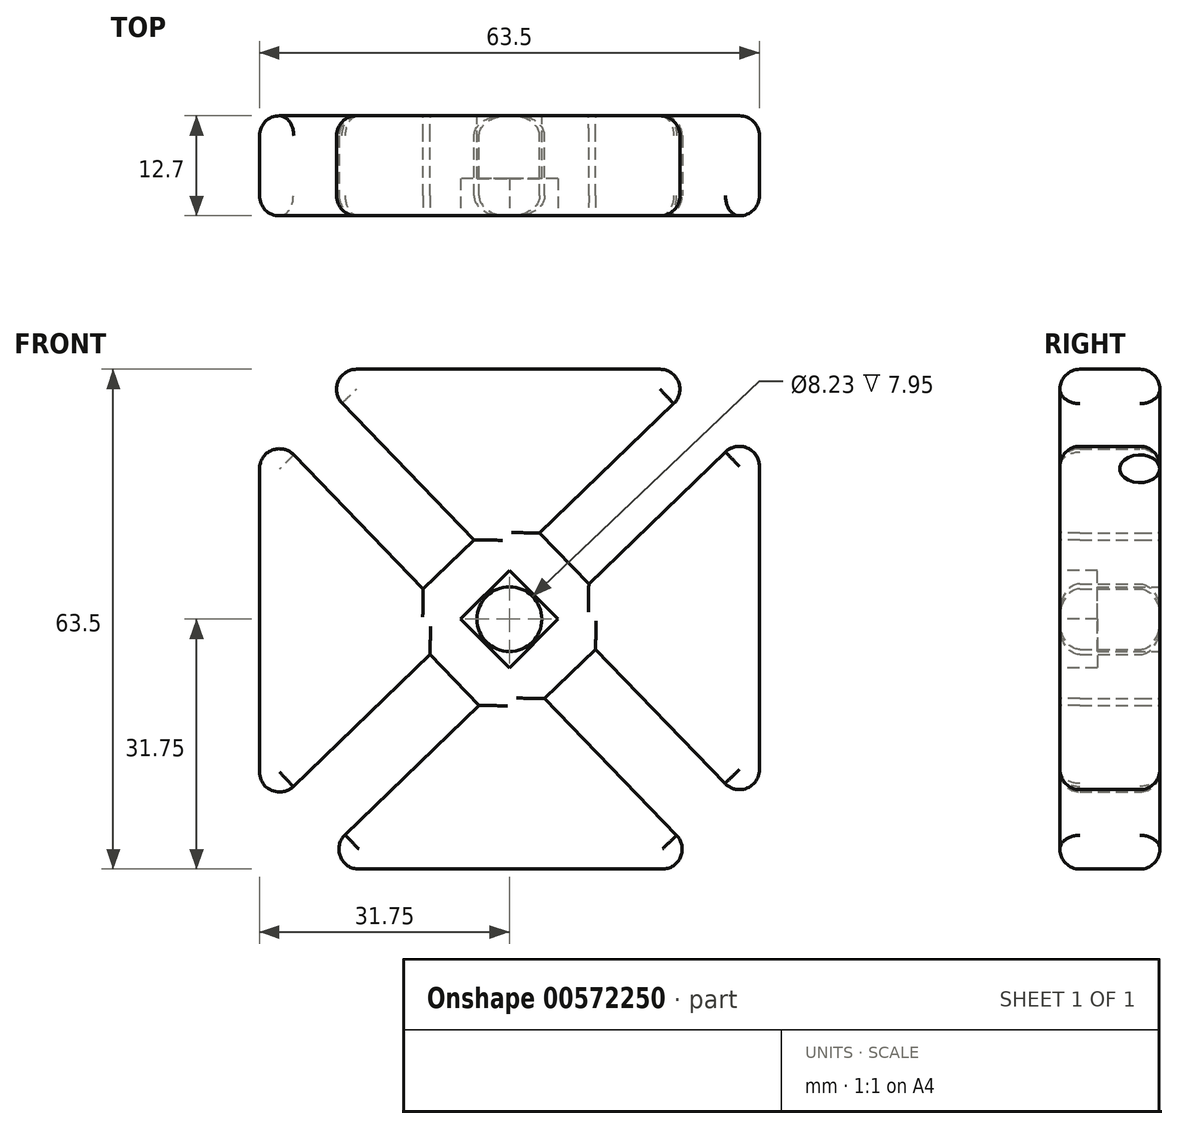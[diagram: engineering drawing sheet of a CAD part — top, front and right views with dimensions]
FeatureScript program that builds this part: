
annotation { "Feature Type Name" : "Feature", "Feature Type Description" : "" }
export const myFeature = defineFeature(function(context is Context, id is Id, definition is map)
    precondition{}
    {
        {
            var Q0;
            Q0=qCreatedBy(makeId("Front.planeOp"),FACE);
            var sketch = newSketch(context, id + "F0", { "sketchPlane" : qUnion([Q0])});
            skLineSegment(sketch, "E0.bottom", {"start": v(0, 0) * mm, "end": v(63.5, 0) * mm});
            skLineSegment(sketch, "E0.top", {"start": v(0, 63.5) * mm, "end": v(63.5, 63.5) * mm});
            skLineSegment(sketch, "E0.left", {"start": v(0, 0) * mm, "end": v(0, 63.5) * mm});
            skLineSegment(sketch, "E0.right", {"start": v(63.5, 0) * mm, "end": v(63.5, 63.5) * mm});
            skCircle(sketch, "E1", {"center": v(31.75, 31.75) * mm, "radius": 4.11 * mm});
            skPoint(sketch, "E1.centerSnap0", {"position": v(0, 31.75) * mm});
            skPoint(sketch, "E1.centerSnap1", {"position": v(31.75, 0) * mm});
            skLineSegment(sketch, "E2", {"start": v(0, 57.15) * mm, "end": v(20.8, 35.6) * mm});
            skLineSegment(sketch, "E3", {"start": v(20.8, 35.6) * mm, "end": v(27.26, 41.83) * mm});
            skLineSegment(sketch, "E4", {"start": v(27.26, 41.83) * mm, "end": v(6.35, 63.5) * mm});
            skPoint(sketch, "E5.startSnap0", {"position": v(63.5, 31.75) * mm});
            skPoint(sketch, "E6.startSnap0", {"position": v(31.75, 63.5) * mm});
            skLineSegment(sketch, "E7.1.0", {"start": v(27.9, 20.8) * mm, "end": v(21.67, 27.26) * mm});
            skLineSegment(sketch, "E7.1.1", {"start": v(21.67, 27.26) * mm, "end": v(0, 6.35) * mm});
            skLineSegment(sketch, "E7.1.2", {"start": v(6.35, 0) * mm, "end": v(27.9, 20.8) * mm});
            skLineSegment(sketch, "E7.2.0", {"start": v(42.7, 27.9) * mm, "end": v(36.24, 21.67) * mm});
            skLineSegment(sketch, "E7.2.1", {"start": v(36.24, 21.67) * mm, "end": v(57.15, 0) * mm});
            skLineSegment(sketch, "E7.2.2", {"start": v(63.5, 6.35) * mm, "end": v(42.7, 27.9) * mm});
            skLineSegment(sketch, "E7.3.0", {"start": v(35.6, 42.7) * mm, "end": v(41.83, 36.24) * mm});
            skLineSegment(sketch, "E7.3.1", {"start": v(41.83, 36.24) * mm, "end": v(63.5, 57.15) * mm});
            skLineSegment(sketch, "E7.3.2", {"start": v(57.15, 63.5) * mm, "end": v(35.6, 42.7) * mm});
            skLineSegment(sketch, "E8", {"start": v(0, 63.5) * mm, "end": v(63.5, 0) * mm, "construction": true});
            skSolve(sketch);
        }
        {
            var Q0;
            Q0=makeQuery(id+"F0.imprint","IMPRINT",FACE,{"disambiguationData":[TD([[makeQuery(id+"F0.imprint","IMPRINT",EDGE,{"derivedFrom":sQuery(id+"F0.wireOp",EDGE,"E1")}),-1.0]])]});
            extrude(context, id + "F1", {"entities" : qUnion([Q0]), "depth" : 12.7 * mm, "offsetDistance" : 25.4 * mm});
        }
        {
            var Q0;
            Q0=makeQuery(id+"F1.opExtrude","CAP_EDGE",EDGE,{"disambiguationData":[OSD([sQuery(id+"F0.wireOp",EDGE,"E0.top")])],"isStart":false});
            var Q1;
            Q1=makeQuery(id+"F1.opExtrude","CAP_EDGE",EDGE,{"disambiguationData":[OSD([sQuery(id+"F0.wireOp",EDGE,"E0.top")])],"isStart":true});
            var Q2;
            Q2=makeQuery(id+"F1.opExtrude","SWEPT_EDGE",EDGE,{"disambiguationData":[OSD([sQuery(id+"F0.wireOp",EDGE,"E0.top"),sQuery(id+"F0.wireOp",EDGE,"f9768a7e-fa62-441e-aa7b-9de3904fa84c0.MirrorCS")])]});
            var Q3;
            Q3=makeQuery(id+"F1.opExtrude","SWEPT_EDGE",EDGE,{"disambiguationData":[OSD([sQuery(id+"F0.wireOp",EDGE,"E0.right"),sQuery(id+"F0.wireOp",EDGE,"4fa41d55-befb-4fce-a351-e9238d651dca0.MirrorCS")])]});
            var Q4;
            Q4=makeQuery(id+"F1.opExtrude","CAP_EDGE",EDGE,{"disambiguationData":[OSD([sQuery(id+"F0.wireOp",EDGE,"f9768a7e-fa62-441e-aa7b-9de3904fa84c0.MirrorCS")])],"isStart":false});
            var Q5;
            Q5=makeQuery(id+"F1.opExtrude","CAP_EDGE",EDGE,{"disambiguationData":[OSD([sQuery(id+"F0.wireOp",EDGE,"4fa41d55-befb-4fce-a351-e9238d651dca0.MirrorCS")])],"isStart":false});
            var Q6;
            Q6=makeQuery(id+"F1.opExtrude","CAP_EDGE",EDGE,{"disambiguationData":[OSD([sQuery(id+"F0.wireOp",EDGE,"fccd8fe7-7fe2-4fae-9692-d2ddfba189940.MirrorCS")])],"isStart":false});
            var Q7;
            Q7=makeQuery(id+"F1.opExtrude","CAP_EDGE",EDGE,{"disambiguationData":[OSD([sQuery(id+"F0.wireOp",EDGE,"E2")])],"isStart":false});
            var Q8;
            Q8=makeQuery(id+"F1.opExtrude","CAP_EDGE",EDGE,{"disambiguationData":[OSD([sQuery(id+"F0.wireOp",EDGE,"E0.right")])],"isStart":false});
            var Q9;
            Q9=makeQuery(id+"F1.opExtrude","CAP_EDGE",EDGE,{"disambiguationData":[OSD([sQuery(id+"F0.wireOp",EDGE,"2e8d7578-45d3-4b48-b28d-f560d07b7ead0.MirrorCS")])],"isStart":false});
            var Q10;
            Q10=makeQuery(id+"F1.opExtrude","CAP_EDGE",EDGE,{"disambiguationData":[OSD([sQuery(id+"F0.wireOp",EDGE,"fcca4da8-b390-416c-8d69-bfd0ada0b1bb0.MirrorCS")])],"isStart":false});
            var Q11;
            Q11=makeQuery(id+"F1.opExtrude","CAP_EDGE",EDGE,{"disambiguationData":[OSD([sQuery(id+"F0.wireOp",EDGE,"6031c4f9-c6bd-4730-b64e-86276a066b080.MirrorCS")])],"isStart":false});
            var Q12;
            Q12=makeQuery(id+"F1.opExtrude","CAP_EDGE",EDGE,{"disambiguationData":[OSD([sQuery(id+"F0.wireOp",EDGE,"E0.bottom")])],"isStart":false});
            var Q13;
            Q13=makeQuery(id+"F1.opExtrude","SWEPT_EDGE",EDGE,{"disambiguationData":[OSD([sQuery(id+"F0.wireOp",EDGE,"E0.bottom"),sQuery(id+"F0.wireOp",EDGE,"2e8d7578-45d3-4b48-b28d-f560d07b7ead0.MirrorCS")])]});
            var Q14;
            Q14=makeQuery(id+"F1.opExtrude","SWEPT_EDGE",EDGE,{"disambiguationData":[OSD([sQuery(id+"F0.wireOp",EDGE,"E0.bottom"),sQuery(id+"F0.wireOp",EDGE,"5bfc7413-cb39-4c83-9fca-94cf49c29bcc0.MirrorCS")])]});
            var Q15;
            Q15=makeQuery(id+"F1.opExtrude","CAP_EDGE",EDGE,{"disambiguationData":[OSD([sQuery(id+"F0.wireOp",EDGE,"E0.bottom")])],"isStart":true});
            var Q16;
            Q16=makeQuery(id+"F1.opExtrude","CAP_EDGE",EDGE,{"disambiguationData":[OSD([sQuery(id+"F0.wireOp",EDGE,"5bfc7413-cb39-4c83-9fca-94cf49c29bcc0.MirrorCS")])],"isStart":false});
            var Q17;
            Q17=makeQuery(id+"F1.opExtrude","CAP_EDGE",EDGE,{"disambiguationData":[OSD([sQuery(id+"F0.wireOp",EDGE,"664e3d7c-05cb-45da-befe-3355a4f8bf300.MirrorCS")])],"isStart":false});
            var Q18;
            Q18=makeQuery(id+"F1.opExtrude","CAP_EDGE",EDGE,{"disambiguationData":[OSD([sQuery(id+"F0.wireOp",EDGE,"884f03f1-4bdd-4ba0-a95d-2b0d860ba54e0.MirrorCS")])],"isStart":false});
            var Q19;
            Q19=makeQuery(id+"F1.opExtrude","CAP_EDGE",EDGE,{"disambiguationData":[OSD([sQuery(id+"F0.wireOp",EDGE,"E0.left")])],"isStart":false});
            var Q20;
            Q20=makeQuery(id+"F1.opExtrude","CAP_EDGE",EDGE,{"disambiguationData":[OSD([sQuery(id+"F0.wireOp",EDGE,"E4")])],"isStart":false});
            var Q21;
            Q21=makeQuery(id+"F1.opExtrude","CAP_EDGE",EDGE,{"disambiguationData":[OSD([sQuery(id+"F0.wireOp",EDGE,"E3")])],"isStart":false});
            var Q22;
            Q22=makeQuery(id+"F1.opExtrude","SWEPT_EDGE",EDGE,{"disambiguationData":[OSD([sQuery(id+"F0.wireOp",EDGE,"E0.left"),sQuery(id+"F0.wireOp",EDGE,"E2")])]});
            var Q23;
            Q23=makeQuery(id+"F1.opExtrude","SWEPT_EDGE",EDGE,{"disambiguationData":[OSD([sQuery(id+"F0.wireOp",EDGE,"E0.top"),sQuery(id+"F0.wireOp",EDGE,"E4")])]});
            var Q24;
            Q24=makeQuery(id+"F1.opExtrude","CAP_EDGE",EDGE,{"disambiguationData":[OSD([sQuery(id+"F0.wireOp",EDGE,"E0.left")])],"isStart":true});
            var Q25;
            Q25=makeQuery(id+"F1.opExtrude","SWEPT_EDGE",EDGE,{"disambiguationData":[OSD([sQuery(id+"F0.wireOp",EDGE,"E0.left"),sQuery(id+"F0.wireOp",EDGE,"884f03f1-4bdd-4ba0-a95d-2b0d860ba54e0.MirrorCS")])]});
            fillet(context, id + "F2", {"entities" : qUnion([Q0, Q1, Q2, Q3, Q4, Q5, Q6, Q7, Q8, Q9, Q10, Q11, Q12, Q13, Q14, Q15, Q16, Q17, Q18, Q19, Q20, Q21, Q22, Q23, Q24, Q25]), "radius" : 2.54 * mm, "tangentPropagation" : true, "allowEdgeOverflow" : false});
        }
        {
            var Q0;
            Q0=makeQuery(id+"F1.opExtrude","SWEPT_FACE",FACE,{"disambiguationData":[OSD([sQuery(id+"F0.wireOp",EDGE,"E0.right")])]});
            var Q1;
            Q1=makeQuery(id+"F1.opExtrude","CAP_EDGE",EDGE,{"disambiguationData":[OSD([sQuery(id+"F0.wireOp",EDGE,"fccd8fe7-7fe2-4fae-9692-d2ddfba189940.MirrorCS")])],"isStart":true});
            var Q2;
            Q2=makeQuery(id+"F1.opExtrude","CAP_EDGE",EDGE,{"disambiguationData":[OSD([sQuery(id+"F0.wireOp",EDGE,"f9768a7e-fa62-441e-aa7b-9de3904fa84c0.MirrorCS")])],"isStart":true});
            var Q3;
            Q3=makeQuery(id+"F1.opExtrude","CAP_EDGE",EDGE,{"disambiguationData":[OSD([sQuery(id+"F0.wireOp",EDGE,"E4")])],"isStart":true});
            var Q4;
            Q4=makeQuery(id+"F1.opExtrude","CAP_EDGE",EDGE,{"disambiguationData":[OSD([sQuery(id+"F0.wireOp",EDGE,"6031c4f9-c6bd-4730-b64e-86276a066b080.MirrorCS")])],"isStart":true});
            var Q5;
            Q5=makeQuery(id+"F1.opExtrude","CAP_EDGE",EDGE,{"disambiguationData":[OSD([sQuery(id+"F0.wireOp",EDGE,"2e8d7578-45d3-4b48-b28d-f560d07b7ead0.MirrorCS")])],"isStart":true});
            var Q6;
            Q6=makeQuery(id+"F1.opExtrude","CAP_EDGE",EDGE,{"disambiguationData":[OSD([sQuery(id+"F0.wireOp",EDGE,"fcca4da8-b390-416c-8d69-bfd0ada0b1bb0.MirrorCS")])],"isStart":true});
            var Q7;
            {var subQ0=sQuery(id+"F0.wireOp",EDGE,"E0.bottom");Q7=makeQuery(id+"F2.opFillet","BLEND_EDGE",EDGE,{"blendedFrom":[makeQuery(id+"F1.opExtrude","CAP_EDGE",EDGE,{"disambiguationData":[OSD([subQ0])],"isStart":true}),makeQuery(id+"F1.opExtrude","CAP_FACE",FACE,{"disambiguationData":[OSD([subQ0,sQuery(id+"F0.wireOp",EDGE,"E0.top"),sQuery(id+"F0.wireOp",EDGE,"E0.left"),sQuery(id+"F0.wireOp",EDGE,"E0.right"),sQuery(id+"F0.wireOp",EDGE,"E1"),sQuery(id+"F0.wireOp",EDGE,"E2"),sQuery(id+"F0.wireOp",EDGE,"E3"),sQuery(id+"F0.wireOp",EDGE,"E4"),sQuery(id+"F0.wireOp",EDGE,"f9768a7e-fa62-441e-aa7b-9de3904fa84c0.MirrorCS"),sQuery(id+"F0.wireOp",EDGE,"4fa41d55-befb-4fce-a351-e9238d651dca0.MirrorCS"),sQuery(id+"F0.wireOp",EDGE,"fccd8fe7-7fe2-4fae-9692-d2ddfba189940.MirrorCS"),sQuery(id+"F0.wireOp",EDGE,"884f03f1-4bdd-4ba0-a95d-2b0d860ba54e0.MirrorCS"),sQuery(id+"F0.wireOp",EDGE,"5bfc7413-cb39-4c83-9fca-94cf49c29bcc0.MirrorCS"),sQuery(id+"F0.wireOp",EDGE,"664e3d7c-05cb-45da-befe-3355a4f8bf300.MirrorCS"),sQuery(id+"F0.wireOp",EDGE,"2e8d7578-45d3-4b48-b28d-f560d07b7ead0.MirrorCS"),sQuery(id+"F0.wireOp",EDGE,"6031c4f9-c6bd-4730-b64e-86276a066b080.MirrorCS"),sQuery(id+"F0.wireOp",EDGE,"fcca4da8-b390-416c-8d69-bfd0ada0b1bb0.MirrorCS")])],"isStart":true})],"blendedInto":[makeQuery(id+"F1.opExtrude","CAP_FACE",FACE,{"disambiguationData":[OSD([subQ0,sQuery(id+"F0.wireOp",EDGE,"E0.top"),sQuery(id+"F0.wireOp",EDGE,"E0.left"),sQuery(id+"F0.wireOp",EDGE,"E0.right"),sQuery(id+"F0.wireOp",EDGE,"E1"),sQuery(id+"F0.wireOp",EDGE,"E2"),sQuery(id+"F0.wireOp",EDGE,"E3"),sQuery(id+"F0.wireOp",EDGE,"E4"),sQuery(id+"F0.wireOp",EDGE,"f9768a7e-fa62-441e-aa7b-9de3904fa84c0.MirrorCS"),sQuery(id+"F0.wireOp",EDGE,"4fa41d55-befb-4fce-a351-e9238d651dca0.MirrorCS"),sQuery(id+"F0.wireOp",EDGE,"fccd8fe7-7fe2-4fae-9692-d2ddfba189940.MirrorCS"),sQuery(id+"F0.wireOp",EDGE,"884f03f1-4bdd-4ba0-a95d-2b0d860ba54e0.MirrorCS"),sQuery(id+"F0.wireOp",EDGE,"5bfc7413-cb39-4c83-9fca-94cf49c29bcc0.MirrorCS"),sQuery(id+"F0.wireOp",EDGE,"664e3d7c-05cb-45da-befe-3355a4f8bf300.MirrorCS"),sQuery(id+"F0.wireOp",EDGE,"2e8d7578-45d3-4b48-b28d-f560d07b7ead0.MirrorCS"),sQuery(id+"F0.wireOp",EDGE,"6031c4f9-c6bd-4730-b64e-86276a066b080.MirrorCS"),sQuery(id+"F0.wireOp",EDGE,"fcca4da8-b390-416c-8d69-bfd0ada0b1bb0.MirrorCS")])],"isStart":true})]});}
            var Q8;
            Q8=makeQuery(id+"F1.opExtrude","CAP_EDGE",EDGE,{"disambiguationData":[OSD([sQuery(id+"F0.wireOp",EDGE,"5bfc7413-cb39-4c83-9fca-94cf49c29bcc0.MirrorCS")])],"isStart":true});
            var Q9;
            Q9=makeQuery(id+"F1.opExtrude","CAP_EDGE",EDGE,{"disambiguationData":[OSD([sQuery(id+"F0.wireOp",EDGE,"664e3d7c-05cb-45da-befe-3355a4f8bf300.MirrorCS")])],"isStart":true});
            var Q10;
            Q10=makeQuery(id+"F1.opExtrude","CAP_EDGE",EDGE,{"disambiguationData":[OSD([sQuery(id+"F0.wireOp",EDGE,"E3")])],"isStart":true});
            var Q11;
            Q11=makeQuery(id+"F1.opExtrude","CAP_EDGE",EDGE,{"disambiguationData":[OSD([sQuery(id+"F0.wireOp",EDGE,"E2")])],"isStart":true});
            var Q12;
            Q12=makeQuery(id+"F1.opExtrude","CAP_EDGE",EDGE,{"disambiguationData":[OSD([sQuery(id+"F0.wireOp",EDGE,"884f03f1-4bdd-4ba0-a95d-2b0d860ba54e0.MirrorCS")])],"isStart":true});
            fillet(context, id + "F3", {"entities" : qUnion([Q0, Q1, Q2, Q3, Q4, Q5, Q6, Q7, Q8, Q9, Q10, Q11, Q12]), "radius" : 2.54 * mm, "tangentPropagation" : true, "allowEdgeOverflow" : false});
        }
        {
            var Q0;
            Q0=makeQuery(id+"F1.opExtrude","CAP_FACE",FACE,{"disambiguationData":[OSD([sQuery(id+"F0.wireOp",EDGE,"E0.bottom"),sQuery(id+"F0.wireOp",EDGE,"E0.top"),sQuery(id+"F0.wireOp",EDGE,"E0.left"),sQuery(id+"F0.wireOp",EDGE,"E0.right"),sQuery(id+"F0.wireOp",EDGE,"E1"),sQuery(id+"F0.wireOp",EDGE,"E2"),sQuery(id+"F0.wireOp",EDGE,"E3"),sQuery(id+"F0.wireOp",EDGE,"E4"),sQuery(id+"F0.wireOp",EDGE,"f9768a7e-fa62-441e-aa7b-9de3904fa84c0.MirrorCS"),sQuery(id+"F0.wireOp",EDGE,"4fa41d55-befb-4fce-a351-e9238d651dca0.MirrorCS"),sQuery(id+"F0.wireOp",EDGE,"fccd8fe7-7fe2-4fae-9692-d2ddfba189940.MirrorCS"),sQuery(id+"F0.wireOp",EDGE,"884f03f1-4bdd-4ba0-a95d-2b0d860ba54e0.MirrorCS"),sQuery(id+"F0.wireOp",EDGE,"5bfc7413-cb39-4c83-9fca-94cf49c29bcc0.MirrorCS"),sQuery(id+"F0.wireOp",EDGE,"664e3d7c-05cb-45da-befe-3355a4f8bf300.MirrorCS"),sQuery(id+"F0.wireOp",EDGE,"2e8d7578-45d3-4b48-b28d-f560d07b7ead0.MirrorCS"),sQuery(id+"F0.wireOp",EDGE,"6031c4f9-c6bd-4730-b64e-86276a066b080.MirrorCS"),sQuery(id+"F0.wireOp",EDGE,"fcca4da8-b390-416c-8d69-bfd0ada0b1bb0.MirrorCS")])],"isStart":false});
            var sketch = newSketch(context, id + "F4", { "sketchPlane" : qUnion([Q0])});
            skLineSegment(sketch, "E9.bottom", {"start": v(37.93, 31.75) * mm, "end": v(31.75, 37.93) * mm});
            skLineSegment(sketch, "E9.top", {"start": v(31.75, 25.57) * mm, "end": v(25.57, 31.75) * mm});
            skLineSegment(sketch, "E9.left", {"start": v(37.93, 31.75) * mm, "end": v(31.75, 25.57) * mm});
            skLineSegment(sketch, "E9.right", {"start": v(31.75, 37.93) * mm, "end": v(25.57, 31.75) * mm});
            skPoint(sketch, "E9.middle", {"position": v(31.75, 31.75) * mm});
            skSolve(sketch);
        }
        {
            var Q0;
            Q0 = qSketchRegion(id + "F4", true);
            extrude(context, id + "F5", {"entities" : qUnion([Q0]), "operationType" : NewBodyOperationType.REMOVE, "oppositeDirection" : true, "depth" : 4.75 * mm, "offsetDistance" : 25.4 * mm});
        }
        {
            var Q0;
            Q0=makeQuery(id+"F1.opExtrude","CAP_EDGE",EDGE,{"disambiguationData":[OSD([sQuery(id+"F0.wireOp",EDGE,"E7.3.2")])],"isStart":true});
            var Q1;
            Q1=makeQuery(id+"F1.opExtrude","CAP_EDGE",EDGE,{"disambiguationData":[OSD([sQuery(id+"F0.wireOp",EDGE,"E7.3.0")])],"isStart":true});
            var Q2;
            Q2=makeQuery(id+"F1.opExtrude","CAP_EDGE",EDGE,{"disambiguationData":[OSD([sQuery(id+"F0.wireOp",EDGE,"E7.2.0")])],"isStart":true});
            var Q3;
            Q3=makeQuery(id+"F1.opExtrude","CAP_EDGE",EDGE,{"disambiguationData":[OSD([sQuery(id+"F0.wireOp",EDGE,"E7.2.1")])],"isStart":true});
            var Q4;
            Q4=makeQuery(id+"F1.opExtrude","CAP_EDGE",EDGE,{"disambiguationData":[OSD([sQuery(id+"F0.wireOp",EDGE,"E7.1.2")])],"isStart":true});
            var Q5;
            Q5=makeQuery(id+"F1.opExtrude","CAP_EDGE",EDGE,{"disambiguationData":[OSD([sQuery(id+"F0.wireOp",EDGE,"E7.1.0")])],"isStart":true});
            var Q6;
            Q6=makeQuery(id+"F1.opExtrude","CAP_EDGE",EDGE,{"disambiguationData":[OSD([sQuery(id+"F0.wireOp",EDGE,"E7.1.1")])],"isStart":true});
            var Q7;
            Q7=makeQuery(id+"F1.opExtrude","CAP_EDGE",EDGE,{"disambiguationData":[OSD([sQuery(id+"F0.wireOp",EDGE,"E7.3.1")])],"isStart":false});
            var Q8;
            Q8=makeQuery(id+"F1.opExtrude","CAP_EDGE",EDGE,{"disambiguationData":[OSD([sQuery(id+"F0.wireOp",EDGE,"E7.3.2")])],"isStart":false});
            var Q9;
            Q9=makeQuery(id+"F1.opExtrude","CAP_EDGE",EDGE,{"disambiguationData":[OSD([sQuery(id+"F0.wireOp",EDGE,"E7.3.0")])],"isStart":false});
            var Q10;
            Q10=makeQuery(id+"F1.opExtrude","CAP_EDGE",EDGE,{"disambiguationData":[OSD([sQuery(id+"F0.wireOp",EDGE,"E7.2.2")])],"isStart":false});
            var Q11;
            Q11=makeQuery(id+"F1.opExtrude","CAP_EDGE",EDGE,{"disambiguationData":[OSD([sQuery(id+"F0.wireOp",EDGE,"E7.2.1")])],"isStart":false});
            var Q12;
            Q12=makeQuery(id+"F1.opExtrude","CAP_EDGE",EDGE,{"disambiguationData":[OSD([sQuery(id+"F0.wireOp",EDGE,"E7.2.0")])],"isStart":false});
            var Q13;
            Q13=makeQuery(id+"F1.opExtrude","CAP_EDGE",EDGE,{"disambiguationData":[OSD([sQuery(id+"F0.wireOp",EDGE,"E7.1.1")])],"isStart":false});
            var Q14;
            Q14=makeQuery(id+"F1.opExtrude","CAP_EDGE",EDGE,{"disambiguationData":[OSD([sQuery(id+"F0.wireOp",EDGE,"E7.1.2")])],"isStart":false});
            var Q15;
            Q15=makeQuery(id+"F1.opExtrude","CAP_EDGE",EDGE,{"disambiguationData":[OSD([sQuery(id+"F0.wireOp",EDGE,"E7.1.0")])],"isStart":false});
            fillet(context, id + "F6", {"entities" : qUnion([Q0, Q1, Q2, Q3, Q4, Q5, Q6, Q7, Q8, Q9, Q10, Q11, Q12, Q13, Q14, Q15]), "radius" : 2.54 * mm, "tangentPropagation" : true, "allowEdgeOverflow" : false});
        }
    });
